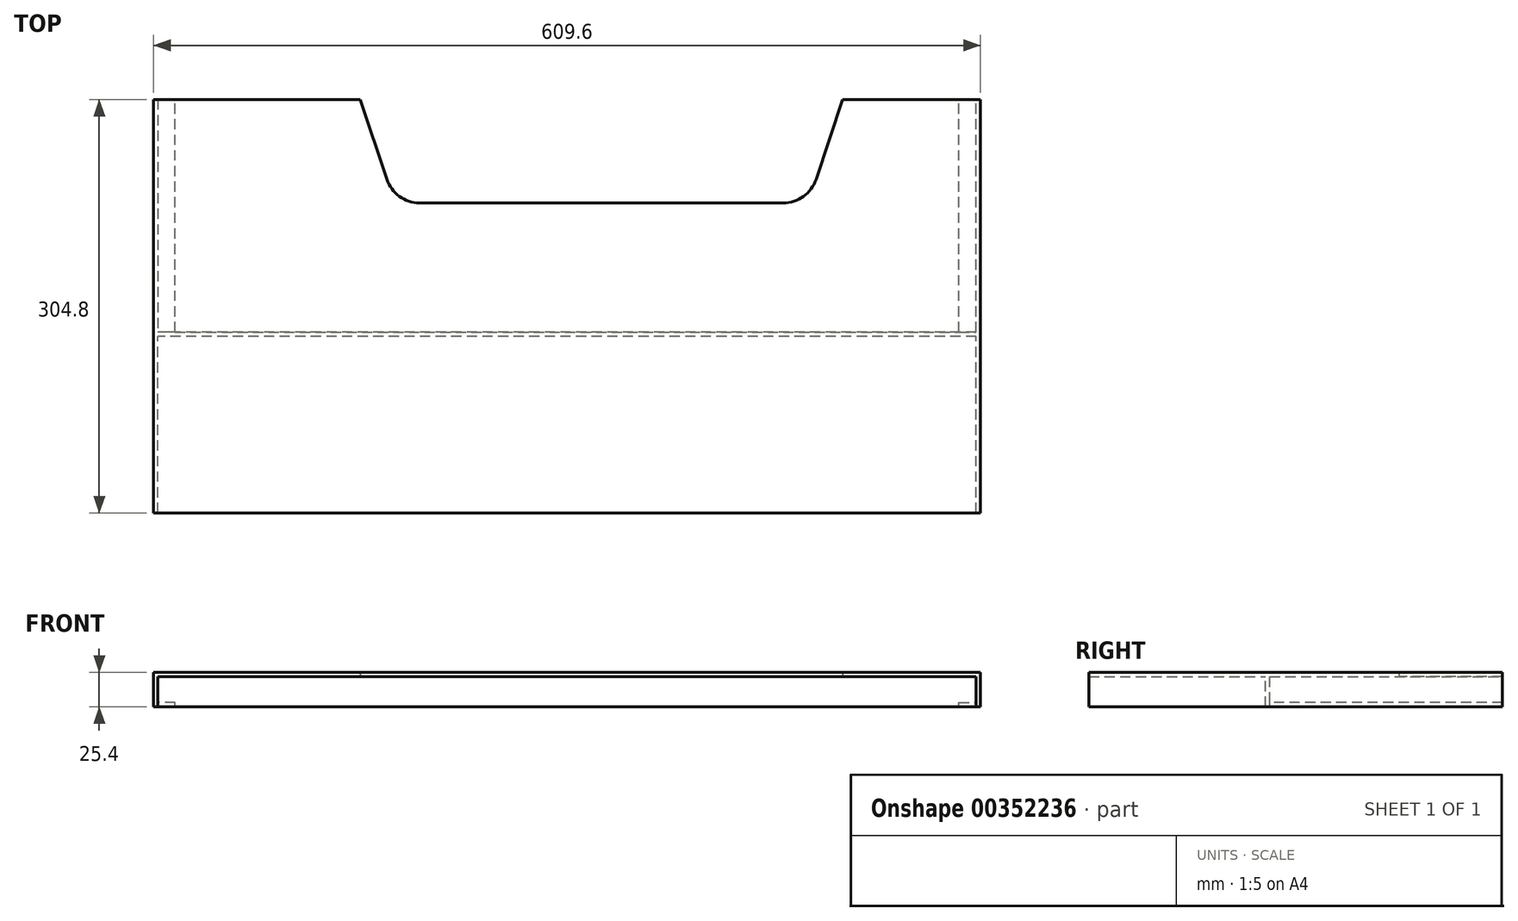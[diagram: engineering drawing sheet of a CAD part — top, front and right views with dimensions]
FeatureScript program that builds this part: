
annotation { "Feature Type Name" : "Feature", "Feature Type Description" : "" }
export const myFeature = defineFeature(function(context is Context, id is Id, definition is map)
    precondition{}
    {
        {
            var Q0;
            Q0=qCreatedBy(makeId("Top.planeOp"),FACE);
            var sketch = newSketch(context, id + "F0", { "sketchPlane" : qUnion([Q0])});
            skLineSegment(sketch, "E0.bottom", {"start": v(0, 0) * mm, "end": v(609.6, 0) * mm});
            skLineSegment(sketch, "E0.top", {"start": v(0, 304.8) * mm, "end": v(152.4, 304.8) * mm});
            skLineSegment(sketch, "E0.left", {"start": v(0, 0) * mm, "end": v(0, 304.8) * mm});
            skLineSegment(sketch, "E0.right", {"start": v(609.6, 0) * mm, "end": v(609.6, 304.8) * mm});
            skLineSegment(sketch, "E1", {"start": v(609.6, 304.8) * mm, "end": v(508, 304.8) * mm});
            skLineSegment(sketch, "E2", {"start": v(464.3, 228.6) * mm, "end": v(196.1, 228.6) * mm});
            skLineSegment(sketch, "E3.trimOffspring", {"start": v(508, 304.8) * mm, "end": v(609.6, 304.8) * mm});
            skLineSegment(sketch, "E4", {"start": v(152.4, 304.8) * mm, "end": v(172.01, 245.97) * mm});
            skLineSegment(sketch, "E5", {"start": v(508, 304.8) * mm, "end": v(488.39, 245.97) * mm});
            skPoint(sketch, "E6.visualSharp", {"position": v(482.6, 228.6) * mm});
            skArc(sketch, "E6.filletArc", {"start": v(464.3, 228.6) * mm, "mid": v(479.14, 233.4) * mm, "end": v(488.39, 245.97) * mm});
            skPoint(sketch, "E7.visualSharp", {"position": v(177.8, 228.6) * mm});
            skArc(sketch, "E7.filletArc", {"start": v(172.01, 245.97) * mm, "mid": v(181.26, 233.4) * mm, "end": v(196.1, 228.6) * mm});
            skSolve(sketch);
        }
        {
            var Q0;
            Q0=makeQuery(id+"F0.imprint","IMPRINT",FACE,{"disambiguationData":[TD([[makeQuery(id+"F0.imprint","IMPRINT",EDGE,{"derivedFrom":sQuery(id+"F0.wireOp",EDGE,"E0.bottom")}),1.0]])]});
            extrude(context, id + "F1", {"entities" : qUnion([Q0]), "depth" : 3.17 * mm});
        }
        {
            var Q0;
            Q0=makeQuery(id+"F0.imprint","IMPRINT",FACE,{"disambiguationData":[TD([[makeQuery(id+"F0.imprint","IMPRINT",EDGE,{"derivedFrom":sQuery(id+"F0.wireOp",EDGE,"E0.bottom")}),1.0]])]});
            var sketch = newSketch(context, id + "F2", { "sketchPlane" : qUnion([Q0])});
            skLineSegment(sketch, "E8.bottom", {"start": v(0, 0) * mm, "end": v(3.17, 0) * mm});
            skLineSegment(sketch, "E8.top", {"start": v(0, 304.8) * mm, "end": v(3.17, 304.8) * mm});
            skLineSegment(sketch, "E8.left", {"start": v(0, 0) * mm, "end": v(0, 304.8) * mm});
            skLineSegment(sketch, "E8.right", {"start": v(3.17, 0) * mm, "end": v(3.17, 304.8) * mm});
            skLineSegment(sketch, "E9.bottom", {"start": v(609.6, 0) * mm, "end": v(606.42, 0) * mm});
            skLineSegment(sketch, "E9.top", {"start": v(609.6, 304.8) * mm, "end": v(606.42, 304.8) * mm});
            skLineSegment(sketch, "E9.left", {"start": v(609.6, 0) * mm, "end": v(609.6, 304.8) * mm});
            skLineSegment(sketch, "E9.right", {"start": v(606.42, 0) * mm, "end": v(606.42, 304.8) * mm});
            skSolve(sketch);
        }
        {
            var Q0;
            Q0 = qSketchRegion(id + "F2", true);
            extrude(context, id + "F3", {"entities" : qUnion([Q0]), "operationType" : NewBodyOperationType.ADD, "oppositeDirection" : true, "depth" : 22.22 * mm});
        }
        {
            var Q0;
            Q0=makeQuery(id+"F3.opExtrude","SWEPT_FACE",FACE,{"disambiguationData":[OSD([sQuery(id+"F2.wireOp",EDGE,"E9.right")])]});
            var sketch = newSketch(context, id + "F4", { "sketchPlane" : qUnion([Q0])});
            skLineSegment(sketch, "E10.bottom", {"start": v(-304.8, -22.23) * mm, "end": v(-133.35, -22.23) * mm});
            skLineSegment(sketch, "E10.top", {"start": v(-304.8, -19.05) * mm, "end": v(-133.35, -19.05) * mm});
            skLineSegment(sketch, "E10.left", {"start": v(-304.8, -22.23) * mm, "end": v(-304.8, -19.05) * mm});
            skLineSegment(sketch, "E10.right", {"start": v(-133.35, -22.23) * mm, "end": v(-133.35, -19.05) * mm});
            skSolve(sketch);
        }
        {
            var Q0;
            Q0=makeQuery(id+"F3.opExtrude","SWEPT_FACE",FACE,{"disambiguationData":[OSD([sQuery(id+"F2.wireOp",EDGE,"E8.right")])]});
            var sketch = newSketch(context, id + "F5", { "sketchPlane" : qUnion([Q0])});
            skLineSegment(sketch, "E11.bottom", {"start": v(304.8, -22.23) * mm, "end": v(133.35, -22.23) * mm});
            skLineSegment(sketch, "E11.top", {"start": v(304.8, -19.05) * mm, "end": v(133.35, -19.05) * mm});
            skLineSegment(sketch, "E11.left", {"start": v(304.8, -22.23) * mm, "end": v(304.8, -19.05) * mm});
            skLineSegment(sketch, "E11.right", {"start": v(133.35, -22.23) * mm, "end": v(133.35, -19.05) * mm});
            skSolve(sketch);
        }
        {
            var Q0;
            Q0=makeQuery(id+"F4.imprint","IMPRINT",FACE,{"disambiguationData":[TD([[makeQuery(id+"F4.imprint","IMPRINT",EDGE,{"derivedFrom":sQuery(id+"F4.wireOp",EDGE,"E10.bottom")}),-1.0]])]});
            extrude(context, id + "F6", {"entities" : qUnion([Q0]), "operationType" : NewBodyOperationType.ADD, "depth" : 12.7 * mm});
        }
        {
            var Q0;
            Q0=makeQuery(id+"F5.imprint","IMPRINT",FACE,{"disambiguationData":[TD([[makeQuery(id+"F5.imprint","IMPRINT",EDGE,{"derivedFrom":sQuery(id+"F5.wireOp",EDGE,"E11.bottom")}),1.0]])]});
            extrude(context, id + "F7", {"entities" : qUnion([Q0]), "operationType" : NewBodyOperationType.ADD, "depth" : 12.7 * mm});
        }
        {
            var Q0;
            Q0=makeQuery(id+"F1.opExtrude","CAP_FACE",FACE,{"disambiguationData":[OSD([sQuery(id+"F0.wireOp",EDGE,"E0.bottom"),sQuery(id+"F0.wireOp",EDGE,"E0.left"),sQuery(id+"F0.wireOp",EDGE,"E0.right"),sQuery(id+"F0.wireOp",EDGE,"E0.top"),sQuery(id+"F0.wireOp",EDGE,"udyLvkZm-oQNg-PUQ1-vq0v-R33SLMlgrAcH"),sQuery(id+"F0.wireOp",EDGE,"NQ6bkSbI-fOjz-fQQp-uYMR-BdPsf8N1QWlK"),sQuery(id+"F0.wireOp",EDGE,"E2"),sQuery(id+"F0.wireOp",EDGE,"E3.trimOffspring")])],"isStart":true});
            var sketch = newSketch(context, id + "F8", { "sketchPlane" : qUnion([Q0])});
            skLineSegment(sketch, "E12.bottom", {"start": v(606.42, -130.17) * mm, "end": v(3.17, -130.18) * mm});
            skLineSegment(sketch, "E12.top", {"start": v(606.42, -133.35) * mm, "end": v(3.17, -133.35) * mm});
            skLineSegment(sketch, "E12.left", {"start": v(606.42, -130.17) * mm, "end": v(606.42, -133.35) * mm});
            skLineSegment(sketch, "E12.right", {"start": v(3.17, -130.18) * mm, "end": v(3.17, -133.35) * mm});
            skSolve(sketch);
        }
        {
            var Q0;
            Q0 = qSketchRegion(id + "F8", true);
            var Q1;
            Q1=makeQuery(id+"F7.boolean.opBoolean","MERGE",FACE,{"derivedFrom":[makeQuery(id+"F3.opExtrude","CAP_FACE",FACE,{"disambiguationData":[OSD([sQuery(id+"F2.wireOp",EDGE,"E8.bottom"),sQuery(id+"F2.wireOp",EDGE,"E8.top"),sQuery(id+"F2.wireOp",EDGE,"E8.left"),sQuery(id+"F2.wireOp",EDGE,"E8.right")])],"isStart":false}),makeQuery(id+"F7.opExtrude","SWEPT_FACE",FACE,{"disambiguationData":[OSD([sQuery(id+"F5.wireOp",EDGE,"E11.bottom")])]})]});
            extrude(context, id + "F9", {"entities" : qUnion([Q0]), "operationType" : NewBodyOperationType.ADD, "endBound" : BoundingType.UP_TO_SURFACE, "endBoundEntityFace" : qUnion([Q1]), "depth" : 25.4 * mm});
        }
    });
